# Revit family: QF_BOURGEAT_3GN_bain_marie mobile_sans_etuve_cuve_separees
name_source: partatom
category: Equipement spécialisé
revit_build: Autodesk Revit 2015 (Build: 20140606_1530(x64)
units: mm (PartAtom-declared; Revit-internal decimal feet)

## types (2) — shared parameters
Charge max = 90.00 kg
Diamètre de Raccordement Evacuation = 27 mm
Fabricant = BOURGEAT
Fréquence = 50 Hz
Hauteur hors tout = 900 mm  [stored 2.95276 ft]
Indice de protection = 33
Intensité nominale = 9 A
Nature isolant = 30mm laine de roche
Phase = 2
Puissance électrique  = 2100 W
Spécification du Fabricant = bain-marie mobiles
Tension = 230 V
URL catalogue = http://www.bourgeat.fr

## per-type parameters (varying)
| type | Longueur hors tout | Modèle | Poids net à vide | Profondeur hors tout | commande_grand_cote | commande_petit_cote | lg_barre_transport |
| commandes_petit_cote | 1280 mm  [stored 4.19948 ft] | 872013 | 60.00 kg | 690 mm  [stored 2.26378 ft] | Non | Oui | 635 mm |
| commande_grand_cote | 1215 mm  [stored 3.98622 ft] | 872313 | 55.00 kg | 755 mm  [stored 2.47703 ft] | Oui | Non | 960 mm  [stored 3.14961 ft] |

note: [stored X ft] marks values corroborated as IEEE doubles in the binary element streams (Revit-internal decimal feet)
